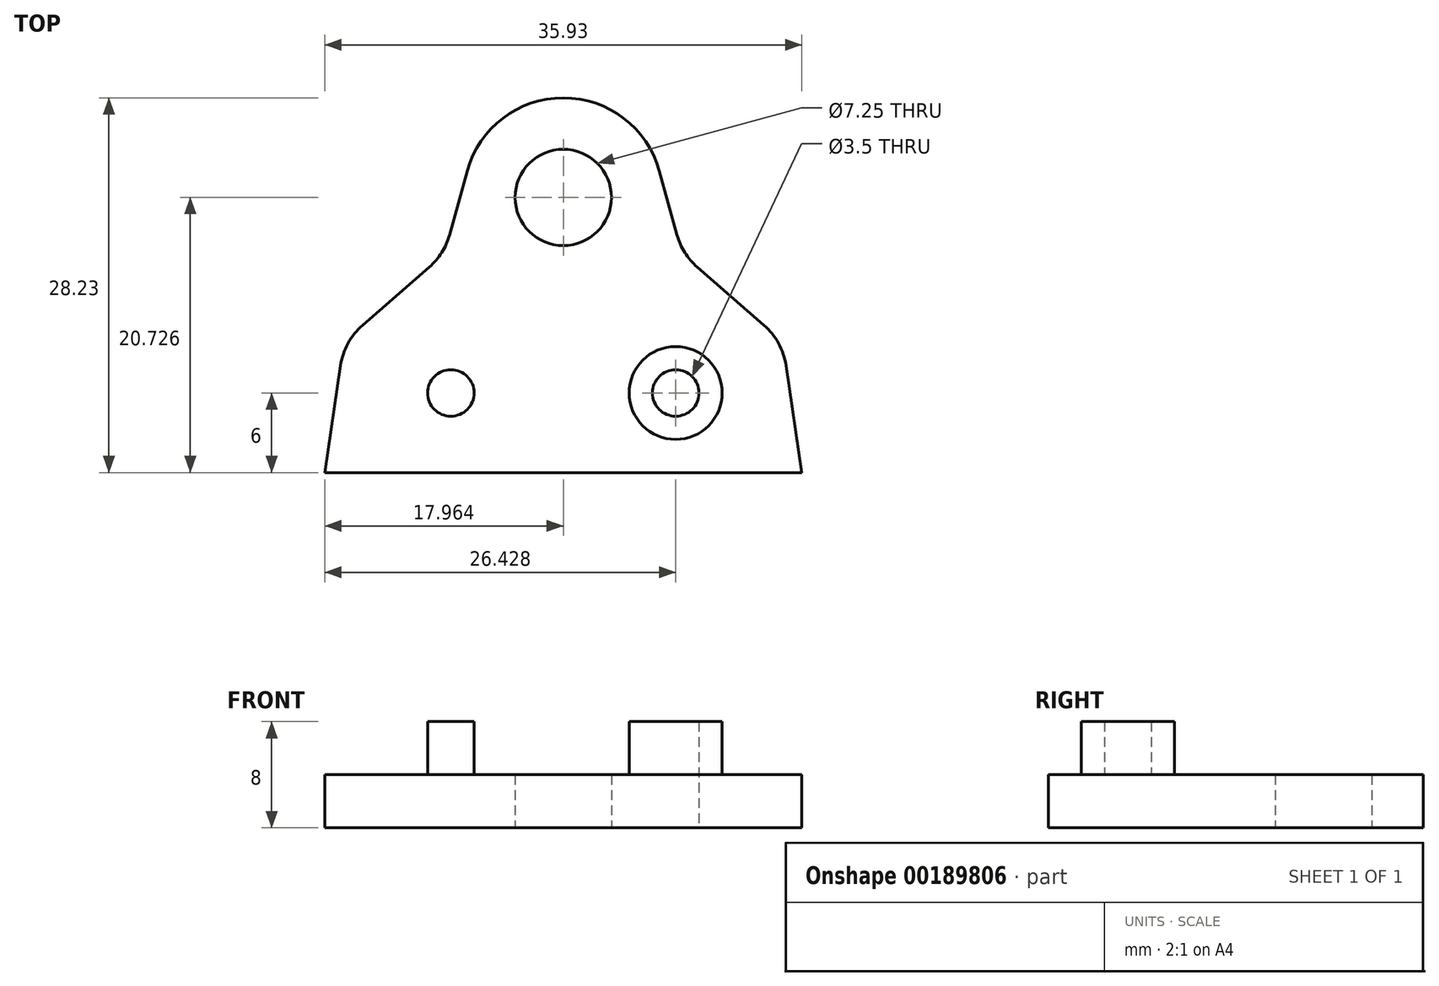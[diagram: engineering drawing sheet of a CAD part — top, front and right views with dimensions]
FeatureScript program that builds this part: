
annotation { "Feature Type Name" : "Feature", "Feature Type Description" : "" }
export const myFeature = defineFeature(function(context is Context, id is Id, definition is map)
    precondition{}
    {
        {
            var Q0;
            Q0=qCreatedBy(makeId("Top.planeOp"),FACE);
            var sketch = newSketch(context, id + "F0", { "sketchPlane" : qUnion([Q0])});
            skLineSegment(sketch, "E0", {"start": v(-19, 0) * mm, "end": v(-17.8, 8.07) * mm});
            skLineSegment(sketch, "E1", {"start": v(-11.13, 15.48) * mm, "end": v(-16.15, 11.1) * mm});
            skCircle(sketch, "E2", {"center": v(-9.5, 6) * mm, "radius": 3.5 * mm});
            skCircle(sketch, "E3", {"center": v(-9.5, 6) * mm, "radius": 1.75 * mm});
            skArc(sketch, "E4", {"start": v(-1.04, 28.23) * mm, "mid": v(-5.58, 26.7) * mm, "end": v(-8.26, 22.73) * mm});
            skLineSegment(sketch, "E5", {"start": v(-9.6, 17.91) * mm, "end": v(-8.26, 22.73) * mm});
            skPoint(sketch, "E6.visualSharp", {"position": v(-10, 16.46) * mm});
            skArc(sketch, "E6.filletArc", {"start": v(-11.13, 15.48) * mm, "mid": v(-10.19, 16.58) * mm, "end": v(-9.6, 17.91) * mm});
            skPoint(sketch, "E7.visualSharp", {"position": v(7.93, 16.46) * mm});
            skArc(sketch, "E8", {"start": v(-1.04, 24.35) * mm, "mid": v(-4.66, 20.73) * mm, "end": v(-1.04, 17.1) * mm});
            skPoint(sketch, "E9.visualSharp", {"position": v(-17.54, 9.9) * mm});
            skArc(sketch, "E9.filletArc", {"start": v(-16.15, 11.1) * mm, "mid": v(-17.25, 9.73) * mm, "end": v(-17.8, 8.07) * mm});
            skPoint(sketch, "E10.visualSharp", {"position": v(15.47, 9.9) * mm});
            skArc(sketch, "E11.MirrorCS", {"start": v(-1.04, 28.23) * mm, "mid": v(3.5, 26.7) * mm, "end": v(6.2, 22.73) * mm});
            skLineSegment(sketch, "E12.MirrorCS", {"start": v(7.53, 17.91) * mm, "end": v(6.2, 22.73) * mm});
            skArc(sketch, "E13.MirrorCS", {"start": v(9.06, 15.48) * mm, "mid": v(8.11, 16.58) * mm, "end": v(7.53, 17.91) * mm});
            skLineSegment(sketch, "E14.MirrorCS", {"start": v(9.06, 15.48) * mm, "end": v(14.08, 11.1) * mm});
            skArc(sketch, "E15.MirrorCS", {"start": v(14.08, 11.1) * mm, "mid": v(15.18, 9.73) * mm, "end": v(15.74, 8.07) * mm});
            skLineSegment(sketch, "E16.MirrorCS", {"start": v(16.93, 0) * mm, "end": v(15.74, 8.07) * mm});
            skArc(sketch, "E17.MirrorCS", {"start": v(-1.04, 24.35) * mm, "mid": v(2.59, 20.73) * mm, "end": v(-1.04, 17.1) * mm});
            skCircle(sketch, "E18.MirrorC", {"center": v(7.43, 6) * mm, "radius": 3.5 * mm});
            skCircle(sketch, "E19.MirrorC", {"center": v(7.43, 6) * mm, "radius": 1.75 * mm});
            skLineSegment(sketch, "E20", {"start": v(-19, 0) * mm, "end": v(16.93, 0) * mm});
            skSolve(sketch);
        }
        {
            var Q0;
            Q0=makeQuery(id+"F0.imprint","IMPRINT",FACE,{"disambiguationData":[TD([[makeQuery(id+"F0.imprint","IMPRINT",EDGE,{"derivedFrom":sQuery(id+"F0.wireOp",EDGE,"Ru46J3V1-BN9A-t4EI-RGMb-jq8WFDNxCXXq")}),-1.0]])]});
            var Q1;
            Q1=makeQuery(id+"F0.imprint","IMPRINT",FACE,{"disambiguationData":[TD([[makeQuery(id+"F0.imprint","IMPRINT",EDGE,{"derivedFrom":sQuery(id+"F0.wireOp",EDGE,"vD3NZcdB-SgQG-xxm7-EOxV-P0EttlGTzlga")}),-1.0]])]});
            var Q2;
            Q2=makeQuery(id+"F0.imprint","IMPRINT",FACE,{"disambiguationData":[TD([[makeQuery(id+"F0.imprint","IMPRINT",EDGE,{"derivedFrom":sQuery(id+"F0.wireOp",EDGE,"E0")}),-1.0]])]});
            extrude(context, id + "F1", {"entities" : qUnion([Q0, Q1, Q2]), "depth" : 4 * mm});
        }
        {
            var Q0;
            Q0=makeQuery(id+"F0.imprint","IMPRINT",FACE,{"disambiguationData":[TD([[makeQuery(id+"F0.imprint","IMPRINT",EDGE,{"derivedFrom":sQuery(id+"F0.wireOp",EDGE,"3bpybDuj-MZcf-nzSA-y5HP-1Ucw2PFUD1lN")}),1.0]])]});
            var Q1;
            Q1=makeQuery(id+"F0.imprint","IMPRINT",FACE,{"disambiguationData":[TD([[makeQuery(id+"F0.imprint","IMPRINT",EDGE,{"derivedFrom":sQuery(id+"F0.wireOp",EDGE,"7a818348-4feb-4938-b127-ce05c0f473900.MirrorC")}),-1.0]])]});
            var Q2;
            Q2=makeQuery(id+"F0.imprint","IMPRINT",FACE,{"disambiguationData":[TD([[makeQuery(id+"F0.imprint","IMPRINT",EDGE,{"derivedFrom":sQuery(id+"F0.wireOp",EDGE,"c41f1a25-7c1b-449b-8bbe-a3a773eef9f20.MirrorC")}),1.0]])]});
            var Q3;
            Q3=makeQuery(id+"F0.imprint","IMPRINT",FACE,{"disambiguationData":[TD([[makeQuery(id+"F0.imprint","IMPRINT",EDGE,{"derivedFrom":sQuery(id+"F0.wireOp",EDGE,"E2")}),1.0]])]});
            var Q4;
            Q4=makeQuery(id+"F0.imprint","IMPRINT",FACE,{"disambiguationData":[TD([[makeQuery(id+"F0.imprint","IMPRINT",EDGE,{"derivedFrom":sQuery(id+"F0.wireOp",EDGE,"YZ3jdz4Q-1nQX-V1tv-PDWv-eDCCawTp6CNW")}),1.0]])]});
            var Q5;
            Q5=makeQuery(id+"F0.imprint","IMPRINT",FACE,{"disambiguationData":[TD([[makeQuery(id+"F0.imprint","IMPRINT",EDGE,{"derivedFrom":sQuery(id+"F0.wireOp",EDGE,"dc8b8af6-f884-4445-9d73-5954fea702aa0.MirrorC")}),1.0]])]});
            var Q6;
            Q6=makeQuery(id+"F0.imprint","IMPRINT",FACE,{"disambiguationData":[TD([[makeQuery(id+"F0.imprint","IMPRINT",EDGE,{"derivedFrom":sQuery(id+"F0.wireOp",EDGE,"E18.MirrorC")}),-1.0]])]});
            extrude(context, id + "F2", {"entities" : qUnion([Q0, Q1, Q2, Q3, Q4, Q5, Q6]), "operationType" : NewBodyOperationType.ADD, "depth" : 4 * mm});
        }
        {
            var Q0;
            Q0=makeQuery(id+"F0.imprint","IMPRINT",FACE,{"disambiguationData":[TD([[makeQuery(id+"F0.imprint","IMPRINT",EDGE,{"derivedFrom":sQuery(id+"F0.wireOp",EDGE,"MXIdjOEz-8Rl6-3WYY-fViL-0X2qQpVSmeco")}),1.0]])]});
            var Q1;
            Q1=makeQuery(id+"F0.imprint","IMPRINT",FACE,{"disambiguationData":[TD([[makeQuery(id+"F0.imprint","IMPRINT",EDGE,{"derivedFrom":sQuery(id+"F0.wireOp",EDGE,"0cc1a50b-0361-4aee-806f-dfb6b972d0bb0.MirrorC")}),-1.0]])]});
            var Q2;
            Q2=makeQuery(id+"F0.imprint","IMPRINT",FACE,{"disambiguationData":[TD([[makeQuery(id+"F0.imprint","IMPRINT",EDGE,{"derivedFrom":sQuery(id+"F0.wireOp",EDGE,"c41f1a25-7c1b-449b-8bbe-a3a773eef9f20.MirrorC")}),-1.0]])]});
            var Q3;
            Q3=makeQuery(id+"F0.imprint","IMPRINT",FACE,{"disambiguationData":[TD([[makeQuery(id+"F0.imprint","IMPRINT",EDGE,{"derivedFrom":sQuery(id+"F0.wireOp",EDGE,"E3")}),1.0]])]});
            var Q4;
            Q4=makeQuery(id+"F0.imprint","IMPRINT",FACE,{"disambiguationData":[TD([[makeQuery(id+"F0.imprint","IMPRINT",EDGE,{"derivedFrom":sQuery(id+"F0.wireOp",EDGE,"pKkQPfjk-ymGL-uVOI-PXtK-5nXTyFiCnjMW")}),1.0]])]});
            var Q5;
            Q5=makeQuery(id+"F0.imprint","IMPRINT",FACE,{"disambiguationData":[TD([[makeQuery(id+"F0.imprint","IMPRINT",EDGE,{"derivedFrom":sQuery(id+"F0.wireOp",EDGE,"dc8b8af6-f884-4445-9d73-5954fea702aa0.MirrorC")}),-1.0]])]});
            var Q6;
            Q6=makeQuery(id+"F0.imprint","IMPRINT",FACE,{"disambiguationData":[TD([[makeQuery(id+"F0.imprint","IMPRINT",EDGE,{"derivedFrom":sQuery(id+"F0.wireOp",EDGE,"E19.MirrorC")}),-1.0]])]});
            extrude(context, id + "F3", {"entities" : qUnion([Q0, Q1, Q2, Q3, Q4, Q5, Q6]), "operationType" : NewBodyOperationType.ADD, "depth" : 8 * mm});
        }
    });
